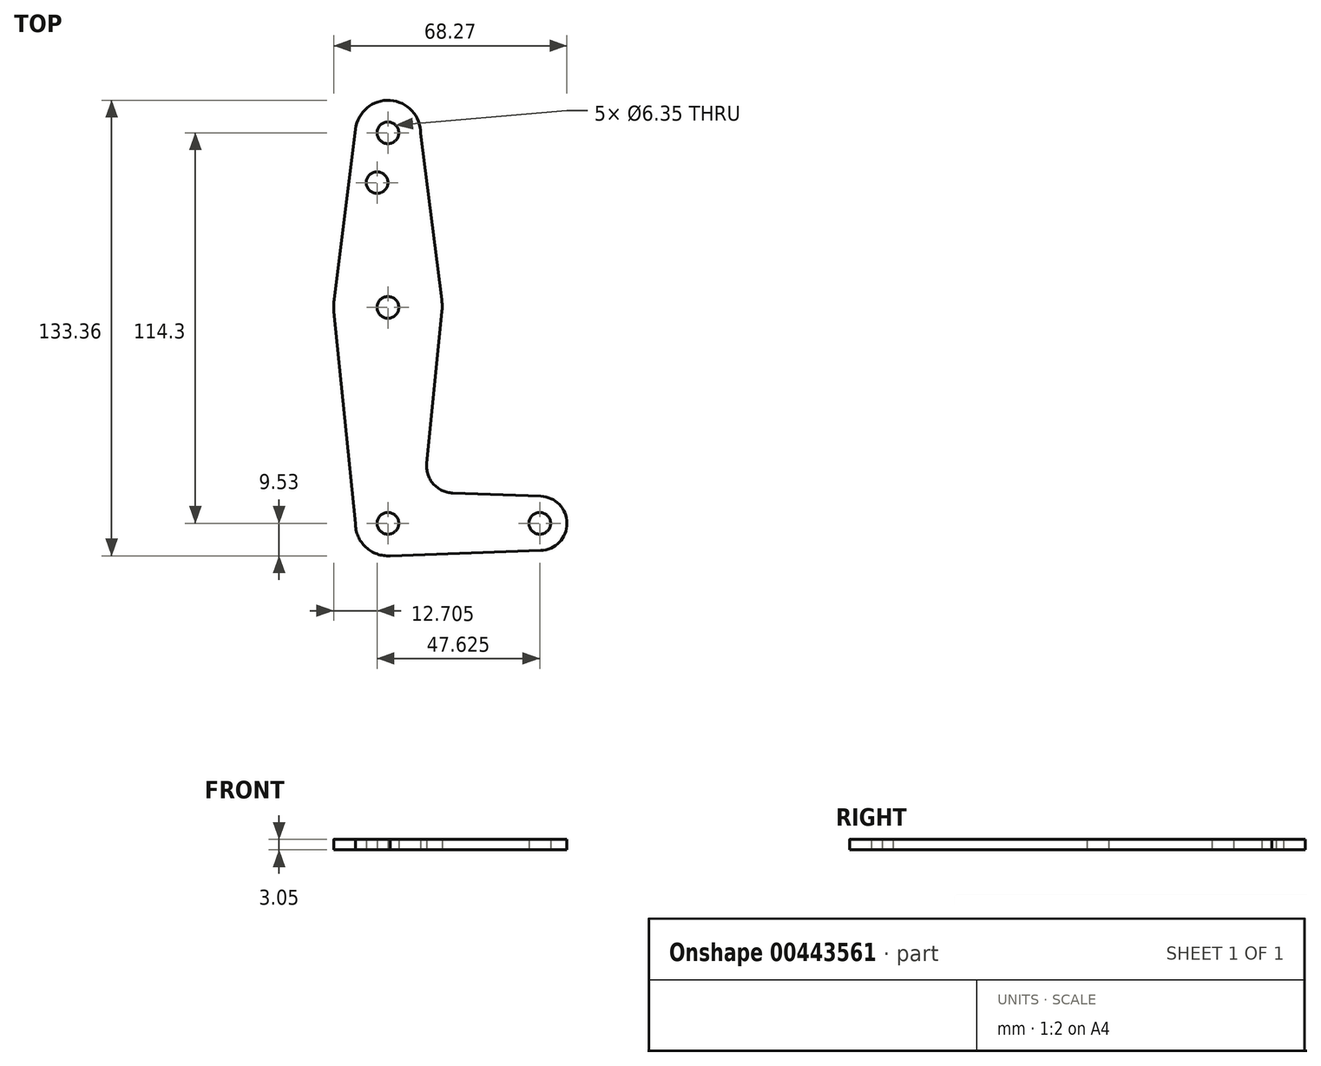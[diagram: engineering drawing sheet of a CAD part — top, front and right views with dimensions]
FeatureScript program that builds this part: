
annotation { "Feature Type Name" : "Feature", "Feature Type Description" : "" }
export const myFeature = defineFeature(function(context is Context, id is Id, definition is map)
    precondition{}
    {
        {
            var Q0;
            Q0=qCreatedBy(makeId("Top.planeOp"),FACE);
            var sketch = newSketch(context, id + "F0", { "sketchPlane" : qUnion([Q0])});
            skLineSegment(sketch, "E0", {"start": v(0, 114.3) * mm, "end": v(0, 0) * mm});
            skCircle(sketch, "E1", {"center": v(0, 114.3) * mm, "radius": 9.53 * mm});
            skCircle(sketch, "E2", {"center": v(0, 63.5) * mm, "radius": 15.88 * mm});
            skLineSegment(sketch, "E3", {"start": v(0, 0) * mm, "end": v(44.45, 0) * mm});
            skCircle(sketch, "E4", {"center": v(0, 0) * mm, "radius": 9.53 * mm});
            skCircle(sketch, "E5", {"center": v(44.45, 0) * mm, "radius": 7.94 * mm});
            skLineSegment(sketch, "E6", {"start": v(-9.46, 115.37) * mm, "end": v(-15.75, 65.48) * mm});
            skLineSegment(sketch, "E7", {"start": v(9.52, 114.09) * mm, "end": v(15.75, 65.52) * mm});
            skLineSegment(sketch, "E8", {"start": v(15.8, 61.91) * mm, "end": v(11.34, 17.59) * mm});
            skLineSegment(sketch, "E9", {"start": v(0, -9.53) * mm, "end": v(44.73, -7.93) * mm});
            skCircle(sketch, "E10", {"center": v(0, 114.3) * mm, "radius": 3.18 * mm});
            skCircle(sketch, "E11", {"center": v(0, 63.2) * mm, "radius": 3.18 * mm});
            skCircle(sketch, "E12", {"center": v(0, 0) * mm, "radius": 3.18 * mm});
            skCircle(sketch, "E13", {"center": v(44.45, 0) * mm, "radius": 3.18 * mm});
            skCircle(sketch, "E14", {"center": v(-3.18, 99.72) * mm, "radius": 3.18 * mm});
            skLineSegment(sketch, "E15", {"start": v(18.97, 8.85) * mm, "end": v(44.75, 7.93) * mm});
            skPoint(sketch, "E16.newPointA", {"position": v(0, 9.53) * mm});
            skPoint(sketch, "E16.newPointB", {"position": v(9.57, 0) * mm});
            skArc(sketch, "E16.filletArc", {"start": v(11.34, 17.59) * mm, "mid": v(13.26, 11.57) * mm, "end": v(18.97, 8.85) * mm});
            skLineSegment(sketch, "E17", {"start": v(-9.53, 0) * mm, "end": v(-15.8, 61.9) * mm});
            skSolve(sketch);
        }
        {
            var Q0;
            Q0 = qSketchRegion(id + "F0", true);
            var Q1;
            {var subQ0=sQuery(id+"F0.wireOp",EDGE,"E4");var subQ1=sQuery(id+"F0.wireOp",EDGE,"E0");var subQ2=makeQuery(id+"F0.imprint","INTERSECT",VERTEX,{"derivedFrom":[subQ1,subQ0]});Q1=makeQuery(id+"F0.imprint","IMPRINT",FACE,{"disambiguationData":[TD([[makeQuery(id+"F0.imprint","IMPRINT",EDGE,{"disambiguationData":[TD([[subQ2,-1.0]])],"derivedFrom":subQ1}),1.0]])]});}
            extrude(context, id + "F1", {"entities" : qUnion([Q0, Q1]), "depth" : 3.05 * mm});
        }
    });
